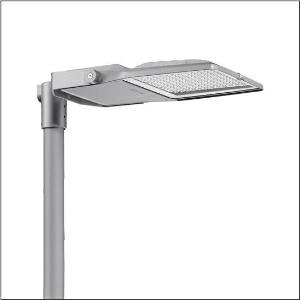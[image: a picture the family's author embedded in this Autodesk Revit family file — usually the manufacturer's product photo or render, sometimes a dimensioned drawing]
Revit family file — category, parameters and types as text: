
# Revit family: floodlight_fl_21_iq_midi___pl43_5xa7782e2a3a_72be
name_source: partatom
category: Lighting Fixtures
units: mm (PartAtom-declared; Revit-internal decimal feet)

## family parameters
Cut with Voids When Loaded = No
Host = Face
Light Source = No
Part Type = Normal
Room Calculation Point = No
Round Connector Dimension = Use Diameter
Shared = No

## types (1)
- --- (1 x LED, 27540 lm, 208.1 W, 3000K)
    Apparent Load = 208 VA
    CIE Flux Codes = 27 78 99 100 100
    Color Rendering = 70
    Color Temperature = 3000K
    Default Elevation = 1800 mm
    Description = Floodlight FL 21 iQ midi, floodlight, primary light control with lens, of PMMA, primary optical cover: protective disc, of toughened safety glass, transparent, light distribution: PL43, light emission: direct distribution, installation type: surface-mounted, LED, High Power LED, rated luminous flux: 27.540lm, luminous efficacy: 132lm/W, light colour: 730, colour temperature: 3000K, control gear: ECG iQ, control: optimised constant luminous flux control (CLO 2.0), Desk-Remote (wireless, voltage-free reading and setting of iQ features in the workshop via application-optimized NFC function/RFID function), Smart-Wire, Night-Set, Temp-Guard, Auto-Match, Street-Remote, with terminal, 6-pole, mains connection: 220..240V, AC, 50/60Hz, start of lifetime: 208W, end of service life: 227W, reduction: 90W, luminaire housing, of diecast aluminium, powder-coated, Siteco® metallic grey (DB 702S), corrosivity category C5 mid according to DIN EN ISO 12944, sealing non-destructively replaceable, please order mast flange separately, mast bracket, of steel, galvanised, powder-coated, Siteco® metallic grey (DB 702S), protection rating (complete): IP66, insulation class (complete): insulation class II (safety insulation), certification: CE, protection symbol: D, impact resistance: IK08, permissible operating ambient temperature: -40..+40°C, permissible operating ambient temperature for outdoor applications: -40..+50°C, standard: DIN EN 12944, LABS conformity tested according to VDMA 24364:2018-05, packaging unit: 1 piece

Light Distribution: PL43
    Height = 76 mm
    Lamp = 1 x LED
    Lamp Light Flux = 27540 lm
    Lamp Power = 208.1 W
    Lamp count = 1
    Length = 657 mm
    Luminous efficacy = 132 lm/W
    Manufacturer = Siteco
    ModVariant = No
    Model = 5XA7782E2A3A
    Number of Poles = 1
    OnlyDefault = Yes
    Power Factor = 1
    Product Name = Floodlight FL 21 iQ midi | PL43
    Product group = floodlight | pylon annexe
    ProductGroupID = 6200
    Protection Class = Protection class II
    Protection Degree = IP 66
    RLX_Detail_Level = 1
    RLX_Emergency_Light_Flux = 0 lm
    RLX_Emergency_Type = 0
    RLX_Emergency_Type_DB = No
    RlxData = <blob elided: 153645 chars, md5=f95a2291>
    Socket = socket
    Standby Power = 0 W
    System Light Flux = 27540 lm
    System Power = 208 W
    Type Comments = factory setting: luminous flux: 100 % | dim-lin: 254 | 710 mA
    Type Image = l_1007123.jpg
    URL = http://relux.com
    VarID = @adj_053471
    Voltage = 0 V
    Weight = 0.00 kg
    Width = 442 mm

## geometry (parser evidence)
native form markers: Blend x4, Sweep x12
no freeform markers — native parametric forms only
